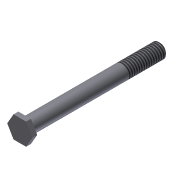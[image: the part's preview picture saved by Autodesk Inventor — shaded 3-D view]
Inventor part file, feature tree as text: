
AUTODESK INVENTOR PART (.ipt)
format: ipt  version: 2013 (Build 170138000, 138)  size: 89,088 bytes
history: native  units: in
note: dims shown in document units (in); Inventor stores cm internally (conversion verified against a paired STEP export)
features: extrude x2, sketch x2, thread x1, chamfer x1
ambient origin geometry x8: Origin, YZ Plane, XZ Plane, XY Plane, X Axis, Y Axis, Z Axis, Center Point
bodies: Solid1 (feature_tree)
feature tree (6):
  extrude  "Extrusion1"  Depth=3.5in TaperAngle=0.0deg
  extrude  "Extrusion2"  Depth=0.125in TaperAngle=0.0deg
  thread  "Thread1"  [1 undecoded]
  chamfer  "Chamfer1"  Distance=0.04in Angle=45.0deg
  sketch  "Sketch1"  dims[d0=0.375in d1=3.5in d2=0.0in]
  sketch  "Sketch2"  dims[d3=0.5625in d4=0.125in d5=0.0in d6=1.0in d7=0.0in d8=0.04in d9=0.125in d10=45.0deg]
note: 1 required parameter value undecoded (feature->parameter linkage not recoverable at this tier; creation-order binding heuristic only, values carry confidence <= 0.55)
